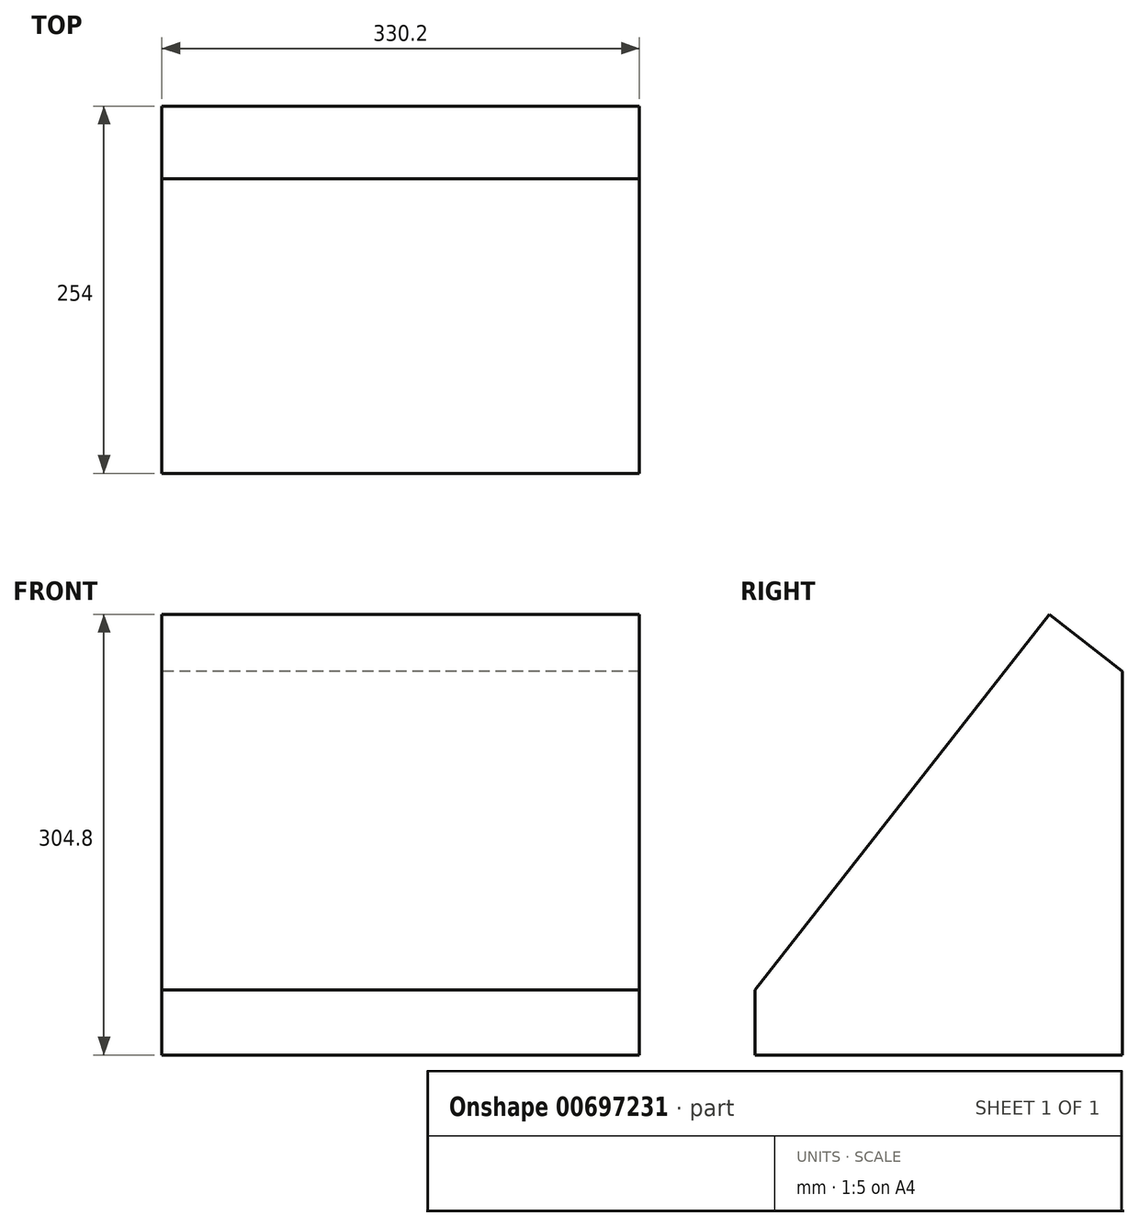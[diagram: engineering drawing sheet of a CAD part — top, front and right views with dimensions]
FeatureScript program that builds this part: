
annotation { "Feature Type Name" : "Feature", "Feature Type Description" : "" }
export const myFeature = defineFeature(function(context is Context, id is Id, definition is map)
    precondition{}
    {
        {
            var Q0;
            Q0=qCreatedBy(makeId("Right.planeOp"),FACE);
            var sketch = newSketch(context, id + "F0", { "sketchPlane" : qUnion([Q0])});
            skLineSegment(sketch, "E0.bottom", {"start": v(-127, -152.4) * mm, "end": v(127, -152.4) * mm});
            skLineSegment(sketch, "E0.top", {"start": v(-127, 152.4) * mm, "end": v(127, 152.4) * mm});
            skLineSegment(sketch, "E0.left", {"start": v(-127, -152.4) * mm, "end": v(-127, 152.4) * mm});
            skLineSegment(sketch, "E0.right", {"start": v(127, -152.4) * mm, "end": v(127, 152.4) * mm});
            skPoint(sketch, "E0.middle", {"position": v(0, 0) * mm});
            skSolve(sketch);
        }
        {
            var Q0;
            Q0=makeQuery(id+"F0.imprint","IMPRINT",FACE,{"disambiguationData":[TD([[makeQuery(id+"F0.imprint","IMPRINT",EDGE,{"derivedFrom":sQuery(id+"F0.wireOp",EDGE,"E0.bottom")}),1.0]])]});
            var sketch = newSketch(context, id + "F1", { "sketchPlane" : qUnion([Q0])});
            skLineSegment(sketch, "E1", {"start": v(-127, -107.58) * mm, "end": v(76.58, 152.4) * mm});
            skLineSegment(sketch, "E2", {"start": v(76.58, 152.4) * mm, "end": v(127, 112.92) * mm});
            skSolve(sketch);
        }
        {
            var Q0;
            {var subQ3=sQuery(id+"F1.wireOp",EDGE,"E1");Q0=makeQuery(id+"F1.imprint","IMPRINT",FACE,{"disambiguationData":[TD([[makeQuery(id+"F1.imprint","IMPRINT",EDGE,{"derivedFrom":subQ3}),-1.0]])]});}
            extrude(context, id + "F2", {"entities" : qUnion([Q0]), "depth" : 330.2 * mm, "offsetDistance" : 25.4 * mm});
        }
    });
